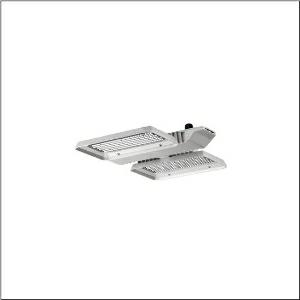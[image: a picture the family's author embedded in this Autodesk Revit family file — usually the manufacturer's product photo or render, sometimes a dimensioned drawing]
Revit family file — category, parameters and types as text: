
# Revit family: highbay_21_51hla1d14fcb
name_source: partatom
category: Lighting Fixtures
units: mm (PartAtom-declared; Revit-internal decimal feet)

## family parameters
Cut with Voids When Loaded = No
Host = Face
Light Source = No
Part Type = Normal
Room Calculation Point = No
Round Connector Dimension = Use Diameter
Shared = No

## types (1)
- --- (1 x LED, 13470 lm, 85.5 W, 4000K)
    Apparent Load = 86 VA
    CIE Flux Codes = 88 95 99 100 99
    Color Rendering = 80
    Color Temperature = 4000K
    Default Elevation = 1800 mm
    Description = Highbay 21, LED high bay luminaire, primary light control with lens, of PMMA, light emission: direct distribution, primary light characteristic: symmetric, installation type: suspended mounting, surface-mounted, for 1x 2 x LED rated luminous flux: 13.470 lm, light colour: 840, colour temperature: 4000K, control gear: ECG DALI, with terminal, 5-pole, max. 2.5mm², mains connection: 230..240V, AC, 50/60Hz, rated input power: 86W, LED unit, of diecast aluminium, unplated, bead blasted, silver, length: 470 mm, width: 500 mm, height: 65mm, housing, of diecast aluminium, uncoated, bead blasted, silver, protection rating (complete): IP65, insulation class (complete): insulation class I (protective earthing), certification: CE, ENEC, VDE, protection symbol: D, impact resistance: IK08 with glass or PC cover, permissible ambient temperature for indoor applications: -35..+45°C, corresponds to IFS (International Featured Standards) requirements for safety and quality in the food industry, reducing of maximum allowable ambient temperature of 5°C with ceiling mounting, packaging unit: 1 piece
    Height = 95 mm
    Lamp = 1 x LED
    Lamp Light Flux = 13470 lm
    Lamp Power = 85.5 W
    Lamp count = 1
    Length = 468 mm
    Luminous efficacy = 158 lm/W
    Manufacturer = Siteco
    ModVariant = No
    Model = 51HLA1D14FCB
    Mounting Place = Ceiling
    Mounting Type = Pendant
    Number of Poles = 1
    OnlyDefault = Yes
    Power Factor = 1
    Product Name = Highbay 21
    Product group = LED high bay luminaire
    ProductGroupID = 903
    Protection Class = Protection class I
    Protection Degree = IP 65
    RLX_Detail_Level = 1
    RlxData = <blob elided: 53909 chars, md5=0123fbcd>
    Socket = socket
    Standby Power = 0 W
    System Light Flux = 13470 lm
    System Power = 86 W
    Type Comments = factory setting: luminous flux: 100 % | dim-lin: 254 | 490 mA
    Type Image = l_1003425.jpg
    URL = http://relux.com
    VarID = @adj_135897
    Voltage = 0 V
    Weight = 0.00 kg
    Width = 501 mm

## geometry (parser evidence)
native form markers: Blend x4, Sweep x12
no freeform markers — native parametric forms only
